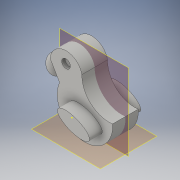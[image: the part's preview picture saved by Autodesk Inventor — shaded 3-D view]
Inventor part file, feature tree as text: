
AUTODESK INVENTOR PART (.ipt)
format: ipt  version: 2016 (Build 200138000, 138)  size: 165,376 bytes
history: native  units: in
note: dims shown in document units (in); Inventor stores cm internally (conversion verified against a paired STEP export)
features: sketch x10, extrude x6, plane x3, mirror x2, other x1
ambient origin geometry x8: Origin, YZ Plane, XZ Plane, XY Plane, X Axis, Y Axis, Z Axis, Center Point
bodies: Solid1 (feature_tree)
feature tree (22):
  extrude  "Extrusion1"  Depth=0.15in TaperAngle=0.0deg
  extrude  "Extrusion3"  Depth=0.0394in TaperAngle=0.0deg
  sketch  "Sketch7"  dims[d6=0.1in d7=0.0in d9=0.0394in d10=0.0in]
  sketch  "Sketch9"  dims[d12=0.1575in d13=0.0687in d14=0.1969in d15=0.0206in]
  sketch  "Sketch10"
  plane  "Work Plane8"
  mirror  "Mirror6"
  plane  "Work Plane9"
  extrude  "Extrusion4"  Depth=0.1969in
  extrude  "Extrusion5"  [1 undecoded]
  mirror  "Mirror7"
  sketch  "Sketch17"
  extrude  "Extrusion6"  [1 undecoded]
  sketch  "Sketch19"
  sketch  "Sketch20"
  extrude  "Extrusion7"  [1 undecoded]
  other  "Duck"
  sketch  "Sketch6"  dims[d0=0.3in d1=0.0in d4=0.15in d5=0.0in]
  sketch  "Sketch11"
  sketch  "Sketch15"
  plane  "Work Plane10"
  sketch  "Sketch18"
note: 3 required parameter values undecoded (feature->parameter linkage not recoverable at this tier; creation-order binding heuristic only, values carry confidence <= 0.55)
